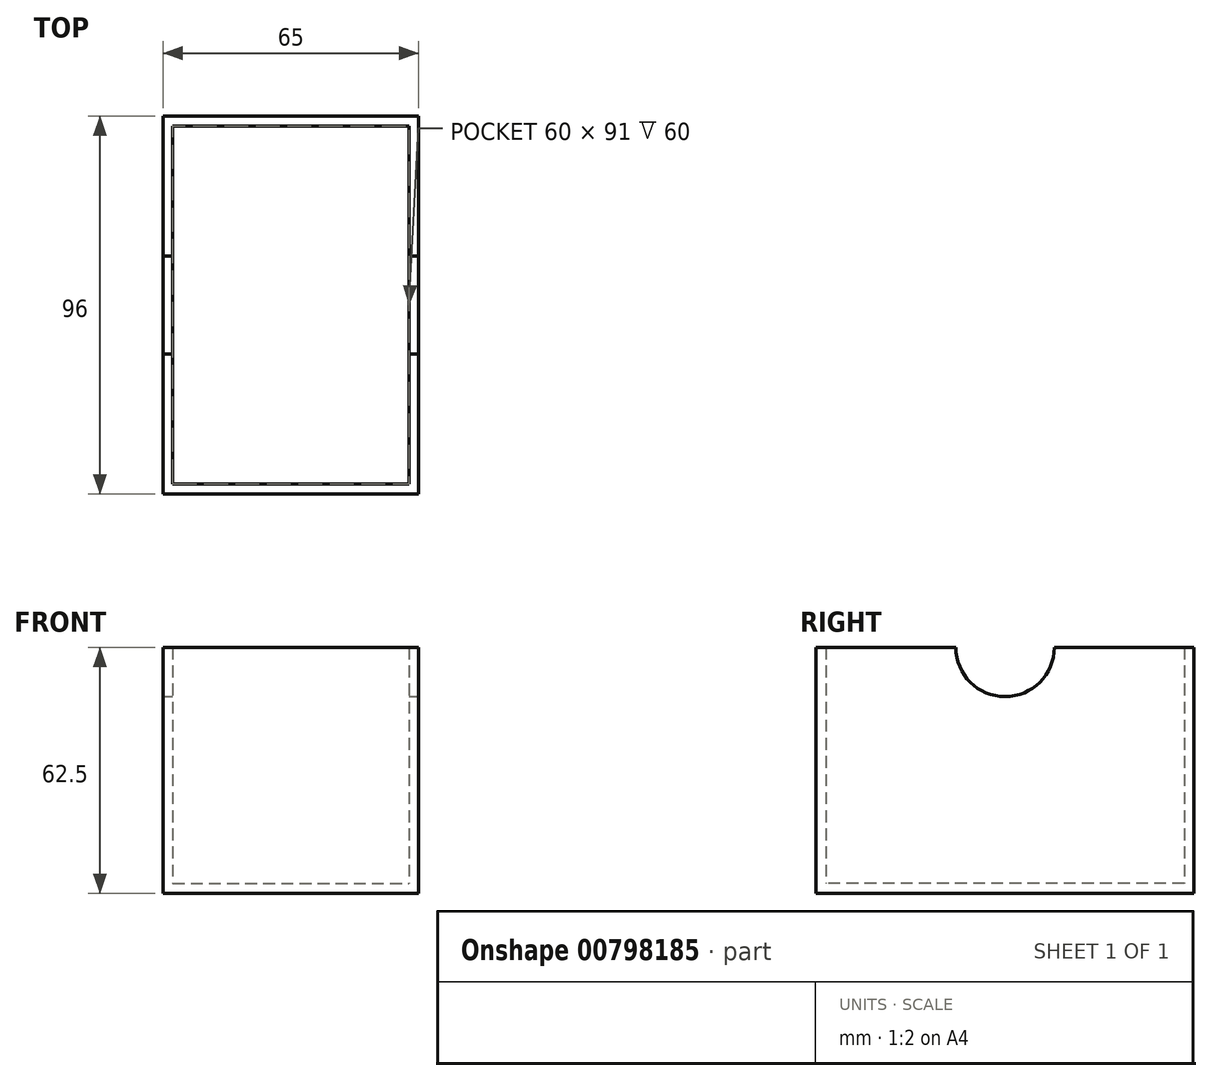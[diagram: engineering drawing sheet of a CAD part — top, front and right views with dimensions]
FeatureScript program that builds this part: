
annotation { "Feature Type Name" : "Feature", "Feature Type Description" : "" }
export const myFeature = defineFeature(function(context is Context, id is Id, definition is map)
    precondition{}
    {
        {
            var Q0;
            Q0=qCreatedBy(makeId("Top.planeOp"),FACE);
            var sketch = newSketch(context, id + "F0", { "sketchPlane" : qUnion([Q0])});
            skLineSegment(sketch, "E0.bottom", {"start": v(-30, 45.5) * mm, "end": v(30, 45.5) * mm});
            skLineSegment(sketch, "E0.top", {"start": v(-30, -45.5) * mm, "end": v(30, -45.5) * mm});
            skLineSegment(sketch, "E0.left", {"start": v(-30, 45.5) * mm, "end": v(-30, -45.5) * mm});
            skLineSegment(sketch, "E0.right", {"start": v(30, 45.5) * mm, "end": v(30, -45.5) * mm});
            skPoint(sketch, "E0.middle", {"position": v(0, 0) * mm});
            skSolve(sketch);
        }
        {
            var Q0;
            Q0 = qSketchRegion(id + "F0", true);
            extrude(context, id + "F1", {"entities" : qUnion([Q0]), "depth" : 60 * mm, "offsetDistance" : 25 * mm});
        }
        {
            var Q0;
            Q0=makeQuery(id+"F1.opExtrude","CAP_FACE",FACE,{"disambiguationData":[OSD([sQuery(id+"F0.wireOp",EDGE,"E0.bottom"),sQuery(id+"F0.wireOp",EDGE,"E0.top"),sQuery(id+"F0.wireOp",EDGE,"E0.left"),sQuery(id+"F0.wireOp",EDGE,"E0.right")])],"isStart":false});
            shell(context, id + "F2", {"entities" : qUnion([Q0]), "thickness" : 2.5 * mm, "oppositeDirection" : true});
        }
        {
            var Q0;
            Q0=makeQuery(id+"F1.opExtrude","SWEPT_FACE",FACE,{"disambiguationData":[OSD([sQuery(id+"F0.wireOp",EDGE,"E0.right")])]});
            var sketch = newSketch(context, id + "F3", { "sketchPlane" : qUnion([Q0])});
            skCircle(sketch, "E1", {"center": v(0, 60) * mm, "radius": 12.5 * mm});
            skSolve(sketch);
        }
        {
            var Q0;
            {var subQ0=sQuery(id+"F3.wireOp",EDGE,"E1");var subQ1=makeQuery(id+"F1.opExtrude","CAP_EDGE",EDGE,{"disambiguationData":[OSD([sQuery(id+"F0.wireOp",EDGE,"E0.right")])],"isStart":false});var subQ2=makeQuery(id+"F3.imprint","INTERSECT",VERTEX,{"disambiguationData":[OD(0.0)],"derivedFrom":[subQ1,subQ0]});Q0=makeQuery(id+"F3.imprint","IMPRINT",FACE,{"disambiguationData":[TD([[makeQuery(id+"F3.imprint","IMPRINT",EDGE,{"disambiguationData":[TD([[subQ2,1.0]])],"derivedFrom":subQ0}),1.0]])]});}
            var Q1;
            Q1=sQuery(id+"F3.wireOp",EDGE,"E1");
            extrude(context, id + "F4", {"entities" : qUnion([Q0]), "operationType" : NewBodyOperationType.REMOVE, "surfaceOperationType" : NewSurfaceOperationType.ADD, "surfaceEntities" : qUnion([Q1]), "endBound" : BoundingType.THROUGH_ALL, "oppositeDirection" : true, "depth" : 143 * mm, "offsetDistance" : 25 * mm});
        }
    });
